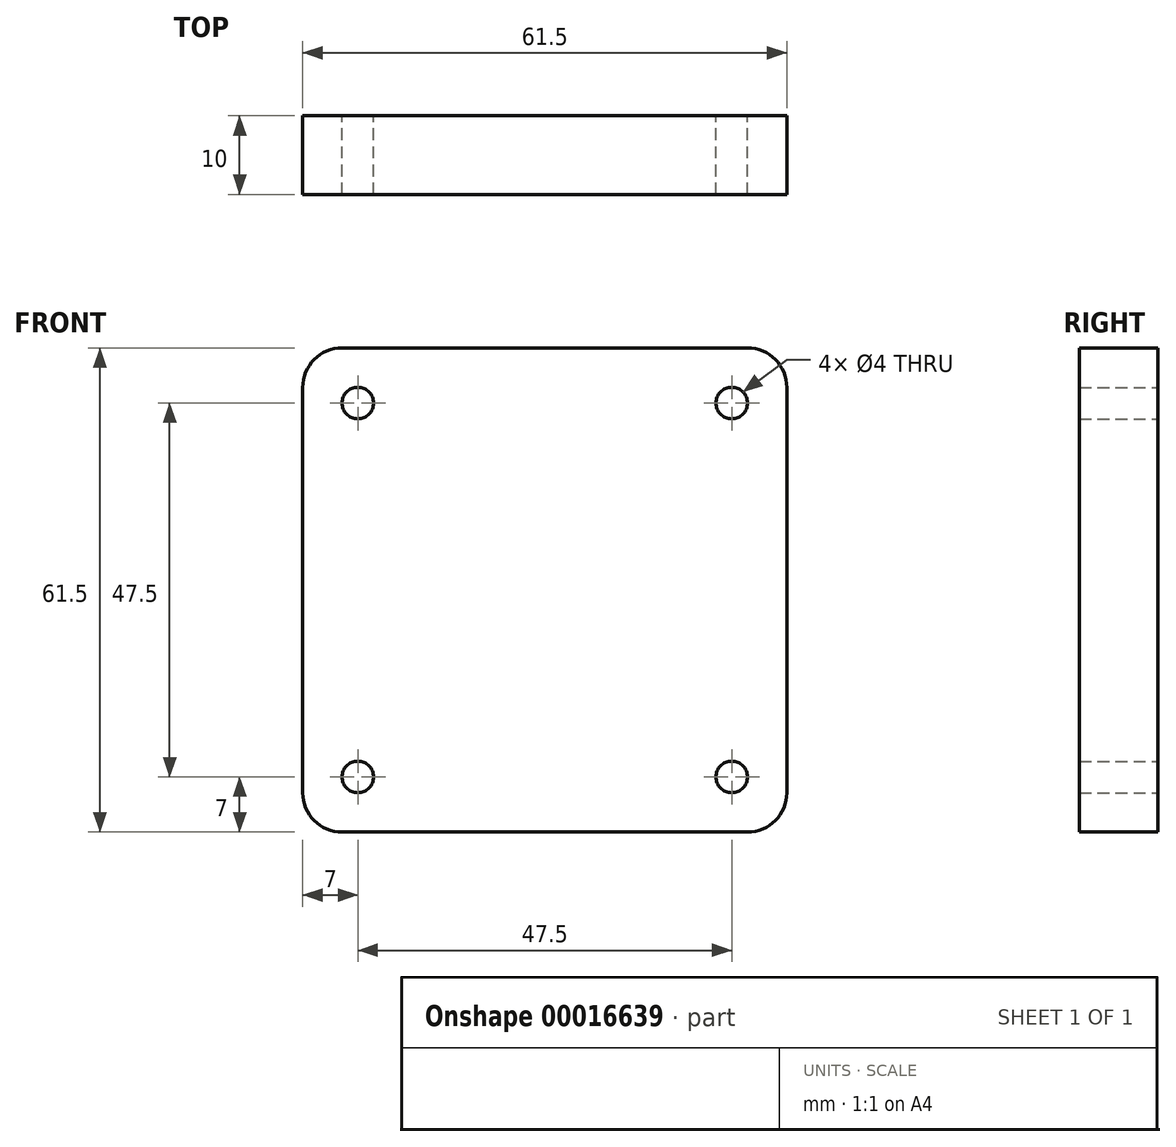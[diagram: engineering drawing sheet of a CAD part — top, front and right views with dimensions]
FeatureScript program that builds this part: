
annotation { "Feature Type Name" : "Feature", "Feature Type Description" : "" }
export const myFeature = defineFeature(function(context is Context, id is Id, definition is map)
    precondition{}
    {
        {
            var Q0;
            Q0=qCreatedBy(makeId("Front.planeOp"),FACE);
            var sketch = newSketch(context, id + "F0", { "sketchPlane" : qUnion([Q0])});
            skLineSegment(sketch, "E0.rect.bottom", {"start": v(25.75, 30.75) * mm, "end": v(-25.75, 30.75) * mm});
            skLineSegment(sketch, "E0.rect.top", {"start": v(25.75, -30.75) * mm, "end": v(-25.75, -30.75) * mm});
            skLineSegment(sketch, "E0.rect.left", {"start": v(30.75, 25.75) * mm, "end": v(30.75, -25.75) * mm});
            skLineSegment(sketch, "E0.rect.right", {"start": v(-30.75, 25.75) * mm, "end": v(-30.75, -25.75) * mm});
            skPoint(sketch, "E0.rect.middle", {"position": v(0, 0) * mm});
            skPoint(sketch, "E1.visualSharp", {"position": v(30.75, 30.75) * mm});
            skArc(sketch, "E1.filletArc", {"start": v(30.75, 25.75) * mm, "mid": v(29.29, 29.29) * mm, "end": v(25.75, 30.75) * mm});
            skPoint(sketch, "E2.visualSharp", {"position": v(30.75, -30.75) * mm});
            skArc(sketch, "E2.filletArc", {"start": v(25.75, -30.75) * mm, "mid": v(29.29, -29.29) * mm, "end": v(30.75, -25.75) * mm});
            skPoint(sketch, "E3.visualSharp", {"position": v(-30.75, -30.75) * mm});
            skArc(sketch, "E3.filletArc", {"start": v(-30.75, -25.75) * mm, "mid": v(-29.29, -29.29) * mm, "end": v(-25.75, -30.75) * mm});
            skPoint(sketch, "E4.visualSharp", {"position": v(-30.75, 30.75) * mm});
            skArc(sketch, "E4.filletArc", {"start": v(-25.75, 30.75) * mm, "mid": v(-29.29, 29.29) * mm, "end": v(-30.75, 25.75) * mm});
            skLineSegment(sketch, "E5.rect.bottom", {"start": v(23.75, 23.75) * mm, "end": v(-23.75, 23.75) * mm, "construction": true});
            skLineSegment(sketch, "E5.rect.top", {"start": v(23.75, -23.75) * mm, "end": v(-23.75, -23.75) * mm, "construction": true});
            skLineSegment(sketch, "E5.rect.left", {"start": v(23.75, 23.75) * mm, "end": v(23.75, -23.75) * mm, "construction": true});
            skLineSegment(sketch, "E5.rect.right", {"start": v(-23.75, 23.75) * mm, "end": v(-23.75, -23.75) * mm, "construction": true});
            skCircle(sketch, "E6", {"center": v(-23.75, 23.75) * mm, "radius": 2 * mm});
            skCircle(sketch, "E7", {"center": v(23.75, 23.75) * mm, "radius": 2 * mm});
            skCircle(sketch, "E8", {"center": v(23.75, -23.75) * mm, "radius": 2 * mm});
            skCircle(sketch, "E9", {"center": v(-23.75, -23.75) * mm, "radius": 2 * mm});
            skSolve(sketch);
        }
        {
            var Q0;
            Q0 = qSketchRegion(id + "F0", true);
            extrude(context, id + "F1", {"entities" : qUnion([Q0]), "depth" : 10 * mm});
        }
    });
